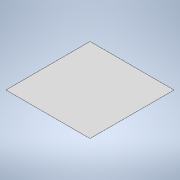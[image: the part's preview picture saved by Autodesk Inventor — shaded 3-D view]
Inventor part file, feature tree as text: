
AUTODESK INVENTOR PART (.ipt)
format: ipt  version: 2020 (Build 240168000, 168)  size: 88,576 bytes
history: native  units: in
note: dims shown in document units (in); Inventor stores cm internally (conversion verified against a paired STEP export)
features: extrude x1, sketch x1
ambient origin geometry x8: Origin, YZ Plane, XZ Plane, XY Plane, X Axis, Y Axis, Z Axis, Center Point
bodies: Solid1 (feature_tree)
feature tree (2):
  extrude  "Extrusion1"  Depth=1.0in
  sketch  "Sketch1"  dims[d0=1.0in d1=1.0in d2=0.001in d3=0.0in]
